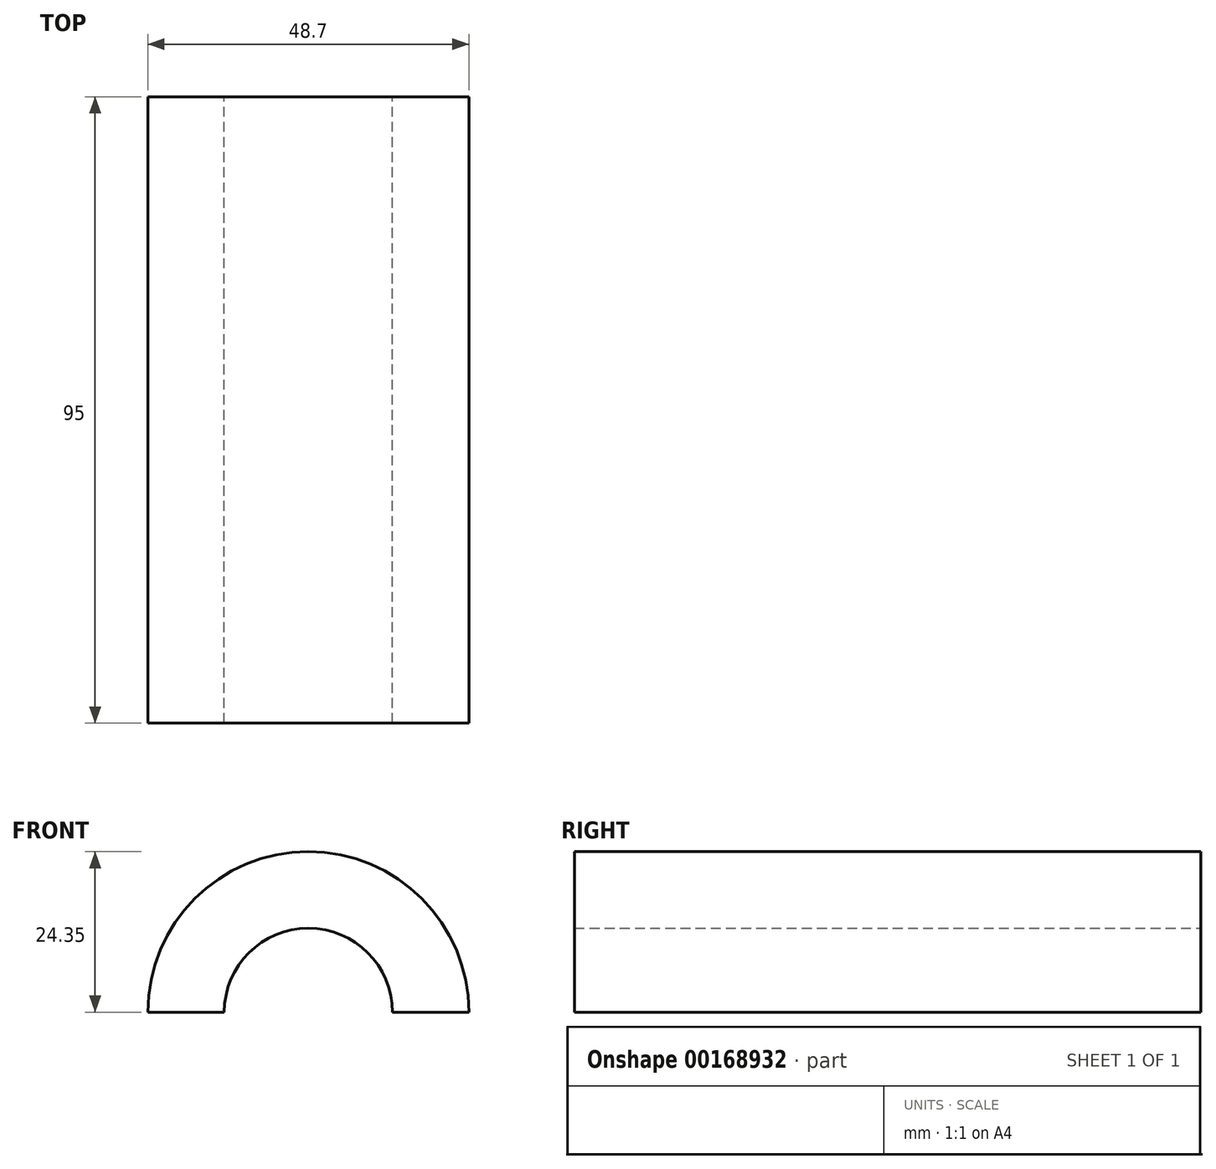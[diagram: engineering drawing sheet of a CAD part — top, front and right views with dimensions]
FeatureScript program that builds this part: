
annotation { "Feature Type Name" : "Feature", "Feature Type Description" : "" }
export const myFeature = defineFeature(function(context is Context, id is Id, definition is map)
    precondition{}
    {
        {
            var Q0;
            Q0=qCreatedBy(makeId("Front.planeOp"),FACE);
            var sketch = newSketch(context, id + "F0", { "sketchPlane" : qUnion([Q0])});
            skArc(sketch, "E0", {"start": v(24.35, 0) * mm, "mid": v(0, 24.35) * mm, "end": v(-24.35, 0) * mm});
            skLineSegment(sketch, "E1", {"start": v(0, 0) * mm, "end": v(-24.35, 0) * mm});
            skLineSegment(sketch, "E2", {"start": v(0, 0) * mm, "end": v(24.35, 0) * mm});
            skArc(sketch, "E3", {"start": v(12.75, 0) * mm, "mid": v(0, 12.75) * mm, "end": v(-12.75, 0) * mm});
            skSolve(sketch);
        }
        {
            var Q0;
            {var subQ0=sQuery(id+"F0.wireOp",EDGE,"E0");Q0=makeQuery(id+"F0.imprint","IMPRINT",FACE,{"disambiguationData":[TD([[makeQuery(id+"F0.imprint","IMPRINT",EDGE,{"derivedFrom":subQ0}),1.0]])]});}
            extrude(context, id + "F1", {"entities" : qUnion([Q0]), "depth" : 95 * mm});
        }
        {
            var Q0;
            Q0=qCreatedBy(makeId("Top.planeOp"),FACE);
            cPlane(context, id + "F2", {"entities" : qUnion([Q0]), "cplaneType" : CPlaneType.OFFSET, "offset" : 24.35 * mm, "width" : 150 * mm, "height" : 150 * mm});
        }
    });
